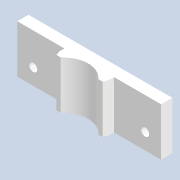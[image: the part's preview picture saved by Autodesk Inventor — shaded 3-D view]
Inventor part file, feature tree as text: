
AUTODESK INVENTOR PART (.ipt)
format: ipt  version: 2020 (Build 240168000, 168)  size: 172,032 bytes
history: native  units: mm
features: extrude x5, sketch x5, chamfer x2, mirror x1, hole x1, projected_geometry x1
ambient origin geometry x8: Origin, YZ Plane, XZ Plane, XY Plane, X Axis, Y Axis, Z Axis, Center Point
bodies: Solid1 (feature_tree)
feature tree (15):
  extrude  "Extrusion1"  Depth=90.0mm
  extrude  "Extrusion2"  Depth=6.0mm
  mirror  "Mirror1"
  extrude  "Extrusion3"  TaperAngle=0.0deg  [1 undecoded]
  chamfer  "Chamfer1"  Distance=1.0mm Angle=45.0deg
  chamfer  "Chamfer2"  Distance=1.0mm Angle=45.0deg
  hole  "Hole1"  [1 undecoded]
  extrude  "Extrusion4"  Depth=3.5mm
  extrude  "Extrusion5"  Depth=10.0mm TaperAngle=0.0deg
  sketch  "Sketch1"  dims[d0=20.0mm d1=90.0mm]
  sketch  "Sketch3"  dims[d2=13.0mm d3=0.0mm d8=6.0mm]
  sketch  "Sketch4"  dims[d9=0.0mm d10=0.0mm d11=0.0mm d12=0.0mm d13=1.0mm d14=3.0mm d15=45.0deg d16=1.0mm d17=3.0mm d18=45.0deg]
  sketch  "Sketch6"  dims[d20=15.5mm d21=31.3mm]
  projected_geometry  "Projected Loop1"
  sketch  "Sketch7"  dims[d22=23.343mm d23=70.0mm d24=5.0mm d25=6.0mm d26=4.0mm d27=2.0mm d28=90.0deg d29=8.0mm d30=20.594885mm d31=10.0mm d32=0.0mm d33=3.5mm d34=3.0mm d35=0.0mm]
note: 2 required parameter values undecoded (feature->parameter linkage not recoverable at this tier; creation-order binding heuristic only, values carry confidence <= 0.55)
